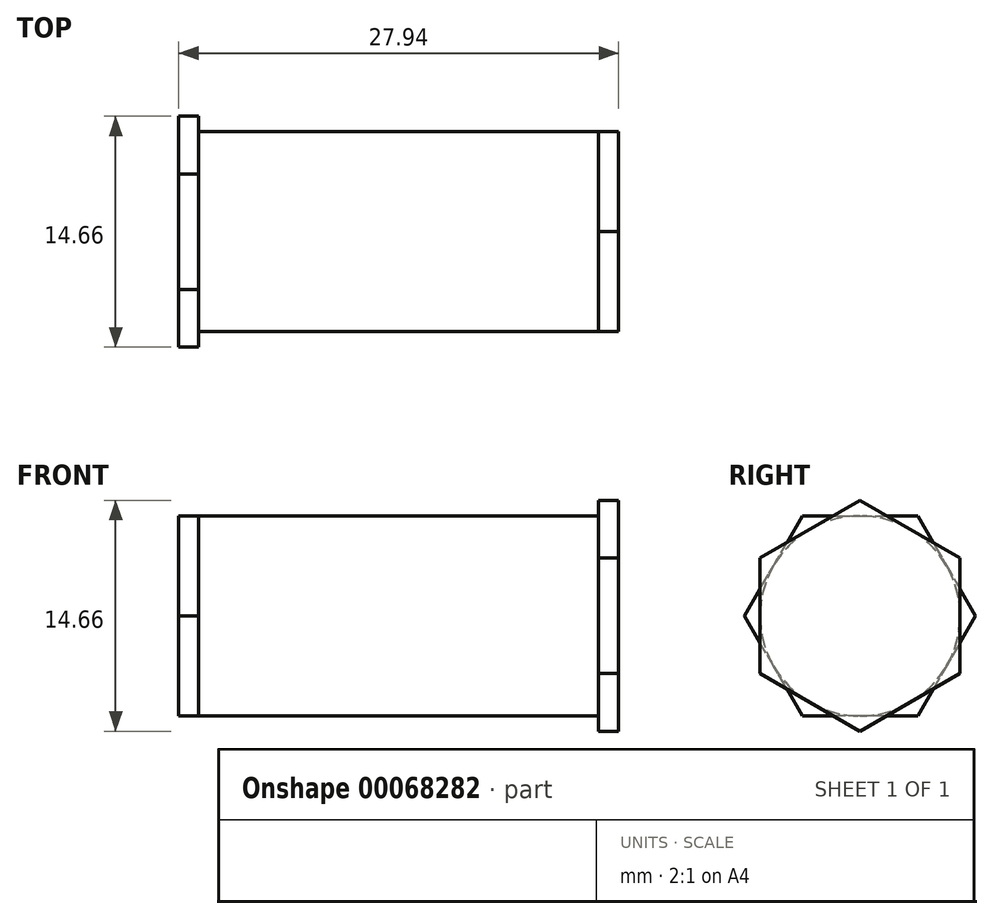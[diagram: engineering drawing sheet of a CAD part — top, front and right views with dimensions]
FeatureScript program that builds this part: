
annotation { "Feature Type Name" : "Feature", "Feature Type Description" : "" }
export const myFeature = defineFeature(function(context is Context, id is Id, definition is map)
    precondition{}
    {
        {
            var Q0;
            Q0=qCreatedBy(makeId("Right.planeOp"),FACE);
            var sketch = newSketch(context, id + "F0", { "sketchPlane" : qUnion([Q0])});
            skCircle(sketch, "E0", {"center": v(0, 0) * mm, "radius": 6.35 * mm});
            skCircle(sketch, "E1.cCircle", {"center": v(0, 0) * mm, "radius": 6.35 * mm, "construction": true});
            skLineSegment(sketch, "E1.0", {"start": v(-3.67, 6.35) * mm, "end": v(3.67, 6.35) * mm});
            skLineSegment(sketch, "E1.1", {"start": v(3.67, 6.35) * mm, "end": v(7.33, 0) * mm});
            skLineSegment(sketch, "E1.2", {"start": v(7.33, 0) * mm, "end": v(3.67, -6.35) * mm});
            skLineSegment(sketch, "E1.3", {"start": v(3.67, -6.35) * mm, "end": v(-3.67, -6.35) * mm});
            skLineSegment(sketch, "E1.4", {"start": v(-3.67, -6.35) * mm, "end": v(-7.33, 0) * mm});
            skLineSegment(sketch, "E1.5", {"start": v(-7.33, 0) * mm, "end": v(-3.67, 6.35) * mm});
            skPoint(sketch, "E1.0.midPoint", {"position": v(0, 6.35) * mm});
            skSolve(sketch);
        }
        {
            var Q0;
            Q0=makeQuery(id+"F0.imprint","IMPRINT",FACE,{"disambiguationData":[TD([[makeQuery(id+"F0.imprint","IMPRINT",EDGE,{"derivedFrom":sQuery(id+"F0.wireOp",EDGE,"E0")}),1.0]])]});
            extrude(context, id + "F1", {"entities" : qUnion([Q0]), "depth" : 25.4 * mm});
        }
        {
            var Q0;
            Q0=makeQuery(id+"F1.opExtrude","CAP_FACE",FACE,{"disambiguationData":[OSD([sQuery(id+"F0.wireOp",EDGE,"E0")])],"isStart":false});
            var sketch = newSketch(context, id + "F2", { "sketchPlane" : qUnion([Q0])});
            skCircle(sketch, "E2.cCircle", {"center": v(0, 0) * mm, "radius": 6.35 * mm, "construction": true});
            skLineSegment(sketch, "E2.0", {"start": v(6.35, 3.67) * mm, "end": v(6.35, -3.67) * mm});
            skLineSegment(sketch, "E2.1", {"start": v(6.35, -3.67) * mm, "end": v(0, -7.33) * mm});
            skLineSegment(sketch, "E2.2", {"start": v(0, -7.33) * mm, "end": v(-6.35, -3.67) * mm});
            skLineSegment(sketch, "E2.3", {"start": v(-6.35, -3.67) * mm, "end": v(-6.35, 3.67) * mm});
            skLineSegment(sketch, "E2.4", {"start": v(-6.35, 3.67) * mm, "end": v(0, 7.33) * mm});
            skLineSegment(sketch, "E2.5", {"start": v(0, 7.33) * mm, "end": v(6.35, 3.67) * mm});
            skPoint(sketch, "E2.0.midPoint", {"position": v(6.35, 0) * mm});
            skSolve(sketch);
        }
        {
            var Q0;
            {var subQ0=makeQuery(id+"F1.opExtrude","CAP_EDGE",EDGE,{"disambiguationData":[OSD([sQuery(id+"F0.wireOp",EDGE,"E0")])],"isStart":false});var subQ6=makeQuery(id+"F2.imprint","INTERSECT",VERTEX,{"derivedFrom":[subQ0,sQuery(id+"F2.wireOp",EDGE,"E2.0")]});Q0=makeQuery(id+"F2.imprint","IMPRINT",FACE,{"disambiguationData":[TD([[makeQuery(id+"F2.imprint","IMPRINT",EDGE,{"disambiguationData":[TD([[subQ6,1.0]])],"derivedFrom":subQ0}),1.0]])]});}
            var Q1;
            {var subQ0=sQuery(id+"F2.wireOp",EDGE,"E2.5");var subQ1=sQuery(id+"F2.wireOp",EDGE,"E2.0");var subQ2=makeQuery(id+"F2.imprint","INTERSECT",VERTEX,{"derivedFrom":[subQ1,subQ0]});Q1=makeQuery(id+"F2.imprint","IMPRINT",FACE,{"disambiguationData":[TD([[makeQuery(id+"F2.imprint","IMPRINT",EDGE,{"disambiguationData":[TD([[subQ2,-1.0]])],"derivedFrom":subQ1}),-1.0]])]});}
            var Q2;
            {var subQ0=sQuery(id+"F2.wireOp",EDGE,"E2.3");var subQ1=sQuery(id+"F2.wireOp",EDGE,"E2.2");var subQ2=makeQuery(id+"F2.imprint","INTERSECT",VERTEX,{"derivedFrom":[subQ1,subQ0]});Q2=makeQuery(id+"F2.imprint","IMPRINT",FACE,{"disambiguationData":[TD([[makeQuery(id+"F2.imprint","IMPRINT",EDGE,{"disambiguationData":[TD([[subQ2,1.0]])],"derivedFrom":subQ1}),-1.0]])]});}
            var Q3;
            {var subQ0=sQuery(id+"F2.wireOp",EDGE,"E2.1");var subQ1=sQuery(id+"F2.wireOp",EDGE,"E2.0");var subQ2=makeQuery(id+"F2.imprint","INTERSECT",VERTEX,{"derivedFrom":[subQ1,subQ0]});Q3=makeQuery(id+"F2.imprint","IMPRINT",FACE,{"disambiguationData":[TD([[makeQuery(id+"F2.imprint","IMPRINT",EDGE,{"disambiguationData":[TD([[subQ2,1.0]])],"derivedFrom":subQ1}),-1.0]])]});}
            var Q4;
            {var subQ0=sQuery(id+"F2.wireOp",EDGE,"E2.5");var subQ1=sQuery(id+"F2.wireOp",EDGE,"E2.4");var subQ2=makeQuery(id+"F2.imprint","INTERSECT",VERTEX,{"derivedFrom":[subQ1,subQ0]});Q4=makeQuery(id+"F2.imprint","IMPRINT",FACE,{"disambiguationData":[TD([[makeQuery(id+"F2.imprint","IMPRINT",EDGE,{"disambiguationData":[TD([[subQ2,1.0]])],"derivedFrom":subQ1}),-1.0]])]});}
            var Q5;
            {var subQ0=sQuery(id+"F2.wireOp",EDGE,"E2.2");var subQ1=sQuery(id+"F2.wireOp",EDGE,"E2.1");var subQ2=makeQuery(id+"F2.imprint","INTERSECT",VERTEX,{"derivedFrom":[subQ1,subQ0]});Q5=makeQuery(id+"F2.imprint","IMPRINT",FACE,{"disambiguationData":[TD([[makeQuery(id+"F2.imprint","IMPRINT",EDGE,{"disambiguationData":[TD([[subQ2,1.0]])],"derivedFrom":subQ1}),-1.0]])]});}
            var Q6;
            {var subQ0=sQuery(id+"F2.wireOp",EDGE,"E2.4");var subQ1=sQuery(id+"F2.wireOp",EDGE,"E2.3");var subQ2=makeQuery(id+"F2.imprint","INTERSECT",VERTEX,{"derivedFrom":[subQ1,subQ0]});Q6=makeQuery(id+"F2.imprint","IMPRINT",FACE,{"disambiguationData":[TD([[makeQuery(id+"F2.imprint","IMPRINT",EDGE,{"disambiguationData":[TD([[subQ2,1.0]])],"derivedFrom":subQ1}),-1.0]])]});}
            extrude(context, id + "F3", {"entities" : qUnion([Q0, Q1, Q2, Q3, Q4, Q5, Q6]), "operationType" : NewBodyOperationType.ADD, "depth" : 1.27 * mm});
        }
        {
            var Q0;
            {var subQ0=sQuery(id+"F0.wireOp",EDGE,"E1.1");var subQ1=sQuery(id+"F0.wireOp",EDGE,"E0");var subQ2=makeQuery(id+"F0.imprint","INTERSECT",VERTEX,{"derivedFrom":[subQ1,subQ0]});Q0=makeQuery(id+"F0.imprint","IMPRINT",FACE,{"disambiguationData":[TD([[makeQuery(id+"F0.imprint","IMPRINT",EDGE,{"disambiguationData":[TD([[subQ2,1.0]])],"derivedFrom":subQ1}),-1.0]])]});}
            var Q1;
            {var subQ0=sQuery(id+"F0.wireOp",EDGE,"E1.5");var subQ1=sQuery(id+"F0.wireOp",EDGE,"E0");var subQ2=makeQuery(id+"F0.imprint","INTERSECT",VERTEX,{"derivedFrom":[subQ1,subQ0]});Q1=makeQuery(id+"F0.imprint","IMPRINT",FACE,{"disambiguationData":[TD([[makeQuery(id+"F0.imprint","IMPRINT",EDGE,{"disambiguationData":[TD([[subQ2,-1.0]])],"derivedFrom":subQ1}),-1.0]])]});}
            var Q2;
            {var subQ0=sQuery(id+"F0.wireOp",EDGE,"E1.0");var subQ1=sQuery(id+"F0.wireOp",EDGE,"E0");var subQ2=makeQuery(id+"F0.imprint","INTERSECT",VERTEX,{"derivedFrom":[subQ1,subQ0]});Q2=makeQuery(id+"F0.imprint","IMPRINT",FACE,{"disambiguationData":[TD([[makeQuery(id+"F0.imprint","IMPRINT",EDGE,{"disambiguationData":[TD([[subQ2,1.0]])],"derivedFrom":subQ1}),-1.0]])]});}
            var Q3;
            {var subQ0=sQuery(id+"F0.wireOp",EDGE,"E1.3");var subQ1=sQuery(id+"F0.wireOp",EDGE,"E0");var subQ2=makeQuery(id+"F0.imprint","INTERSECT",VERTEX,{"derivedFrom":[subQ1,subQ0]});Q3=makeQuery(id+"F0.imprint","IMPRINT",FACE,{"disambiguationData":[TD([[makeQuery(id+"F0.imprint","IMPRINT",EDGE,{"disambiguationData":[TD([[subQ2,-1.0]])],"derivedFrom":subQ1}),-1.0]])]});}
            var Q4;
            {var subQ0=sQuery(id+"F0.wireOp",EDGE,"E1.0");var subQ1=sQuery(id+"F0.wireOp",EDGE,"E0");var subQ2=makeQuery(id+"F0.imprint","INTERSECT",VERTEX,{"derivedFrom":[subQ1,subQ0]});Q4=makeQuery(id+"F0.imprint","IMPRINT",FACE,{"disambiguationData":[TD([[makeQuery(id+"F0.imprint","IMPRINT",EDGE,{"disambiguationData":[TD([[subQ2,-1.0]])],"derivedFrom":subQ1}),-1.0]])]});}
            var Q5;
            {var subQ0=sQuery(id+"F0.wireOp",EDGE,"E1.4");var subQ1=sQuery(id+"F0.wireOp",EDGE,"E0");var subQ2=makeQuery(id+"F0.imprint","INTERSECT",VERTEX,{"derivedFrom":[subQ1,subQ0]});Q5=makeQuery(id+"F0.imprint","IMPRINT",FACE,{"disambiguationData":[TD([[makeQuery(id+"F0.imprint","IMPRINT",EDGE,{"disambiguationData":[TD([[subQ2,-1.0]])],"derivedFrom":subQ1}),-1.0]])]});}
            var Q6;
            {var subQ0=sQuery(id+"F0.wireOp",EDGE,"E0");var subQ4=makeQuery(id+"F0.imprint","INTERSECT",VERTEX,{"derivedFrom":[subQ0,sQuery(id+"F0.wireOp",EDGE,"E1.0")]});Q6=makeQuery(id+"F0.imprint","IMPRINT",FACE,{"disambiguationData":[TD([[makeQuery(id+"F0.imprint","IMPRINT",EDGE,{"disambiguationData":[TD([[subQ4,1.0]])],"derivedFrom":subQ0}),1.0]])]});}
            extrude(context, id + "F4", {"entities" : qUnion([Q0, Q1, Q2, Q3, Q4, Q5, Q6]), "operationType" : NewBodyOperationType.ADD, "oppositeDirection" : true, "depth" : 1.27 * mm});
        }
    });
